# Revit family: Shinhoo_Basic_S_G
name_source: partatom
category: Оборудование
units: mm (PartAtom-declared; Revit-internal decimal feet)

## family parameters
Всегда вертикально = Нет
Классификация = Нет
На основе рабочей плоскости = Нет
Общий = Нет
При загрузке вырезать с полостями = Нет
Размер круглого соединителя = Использовать диаметр
Тип детали = Вставляется
Точка расчета площади = Нет

## types (8) — shared parameters
ADSK_URL страницы изделия = https://shinhoopump.ru
ADSK_Версия Revit = 2019
ADSK_Версия семейства = 1.0
ADSK_Единица измерения = шт
ADSK_Завод-изготовитель = Shinhoo
ADSK_Количество = 1
ADSK_Коэффициент мощности = 1
ADSK_Материал = Чугун с катафорезным покрытием
ADSK_Напряжение = 230 В
ADSK_Обозначение = ГОСТ 31839-2012, ГОСТ 12.2.007.0-75, ГОСТ 12.2.003-91, ГОСТ Р МЭК 60204-1-2007,  ГОСТ 30804
URL = https://shinhoopump.ru
d1 = 33 мм
d6 = 40 мм
r1 = 17 мм
r1_1 = 18 мм
r1_3 = 25 мм
r6 = 20 мм
Изготовитель = Shinhoo
Класс защиты (IP) = IP44
Разработчик = ООО ПРОРУБИМ
Разработчик (телефон) = +7(495)649-85-43
Скорость вращения = 2850
Степень защиты от удара (IK) = IK04
Тип Насоса = Стандартный циркуляционный насос с «мокрым» ротором
Тип основания = встроенный

## per-type parameters (varying)
| type | ADSK_Код изделия | ADSK_Масса | ADSK_Масса_Текст | ADSK_Наименование | ADSK_Наименование краткое | ADSK_Номинальная мощность | ADSK_Полная мощность | ADSK_Расход жидкости | ADSK_Ток | B | B1 | B2 | DN | H | H1 | H2 | L | b1_20 | Группа модели |
| BASIC S 25-4S 180 1x230В - 71211001 | 71211001 | 2.4 | 2.4 | Стандартный циркуляционный насос с «мокрым» ротором BASIC S 25-4S 180 1x230В | BASIC S 25-4S 180 1x230В | 50 Вт | 50 В·А | 0.001000 м³/с | 0 А | 130 мм | 82 мм | 48 мм | 25 мм | 130 мм | 25 мм | 105 мм | 180 мм | 41 мм | BASIC S 25-4S |
| BASIC S 25-6S 130 1x230В - 71211007 | 71211007 | 2.6 | 2.6 | Стандартный циркуляционный насос с «мокрым» ротором BASIC S 25-6S 130 1x230В | BASIC S 25-6S 130 1x230В | 70 Вт | 70 В·А | 0.001167 м³/с | 0 А | 130 мм | 82 мм | 48 мм | 25 мм | 130 мм | 25 мм | 105 мм | 130 мм | 41 мм | BASIC S 25-6S |
| BASIC S 25-6S 180 1x230В - 71211002 | 71211002 | 2.6 | 2.6 | Стандартный циркуляционный насос с «мокрым» ротором BASIC S 25-6S 180 1x230В | BASIC S 25-6S 180 1x230В | 70 Вт | 70 В·А | 0.001167 м³/с | 0 А | 130 мм | 82 мм | 48 мм | 25 мм | 130 мм | 25 мм | 105 мм | 180 мм | 41 мм | BASIC S 25-6S |
| BASIC S 25-8S 180 1x230В - 71211003 | 71211003 | 4.8 | 4.8 | Стандартный циркуляционный насос с «мокрым» ротором BASIC S 25-8S 180 1x230В | BASIC S 25-8S 180 1x230В | 180 Вт | 180 В·А | 0.002583 м³/с | 1 А | 150 мм | 92 мм | 58 мм | 25 мм | 160 мм | 30 мм | 130 мм | 180 мм | 50 мм | BASIC S 25-8S |
| BASIC S 32-4S 180 1x230В - 71211004 | 71211004 | 2.7 | 2.7 | Стандартный циркуляционный насос с «мокрым» ротором BASIC S 32-4S 180 1x230В | BASIC S 32-4S 180 1x230В | 50 Вт | 50 В·А | 0.001111 м³/с | 0 А | 130 мм | 82 мм | 48 мм | 32 мм | 130 мм | 25 мм | 105 мм | 180 мм | 41 мм | BASIC S 32-4S |
| BASIC S 32-6S 180 1x230В - 71211005 | 71211005 | 2.9 | 2.9 | Стандартный циркуляционный насос с «мокрым» ротором BASIC S 32-6S 180 1x230В | BASIC S 32-6S 180 1x230В | 70 Вт | 70 В·А | 0.001389 м³/с | 0 А | 130 мм | 82 мм | 48 мм | 32 мм | 130 мм | 25 мм | 105 мм | 180 мм | 41 мм | BASIC S 32-6S |
| BASIC S 32-8S 180 1x230В - 71211006 | 71211006 | 4.6 | 4.6 | Стандартный циркуляционный насос с «мокрым» ротором BASIC S 32-8S 180 1x230В | BASIC S 32-8S 180 1x230В | 180 Вт | 180 В·А | 0.002583 м³/с | 1 А | 150 мм | 92 мм | 58 мм | 32 мм | 170 мм | 40 мм | 130 мм | 180 мм | 50 мм | BASIC S 32-8S |
| BASIC S 15-6S 130 1x230V - 71211012 | 71211012 | 2.6 | 2.6 | Стандартный циркуляционный насос с «мокрым» ротором BASIC S 15-6S 130 1x230В | BASIC S 15-6S 130 1x230V | 70 Вт | 70 В·А | 0.001167 м³/с | 0 А | 130 мм | 82 мм | 48 мм | 15 мм | 130 мм | 25 мм | 105 мм | 130 мм | 41 мм | BASIC S 25-6S |

## geometry (parser evidence)
native form markers: Sweep x2
no freeform markers — native parametric forms only
